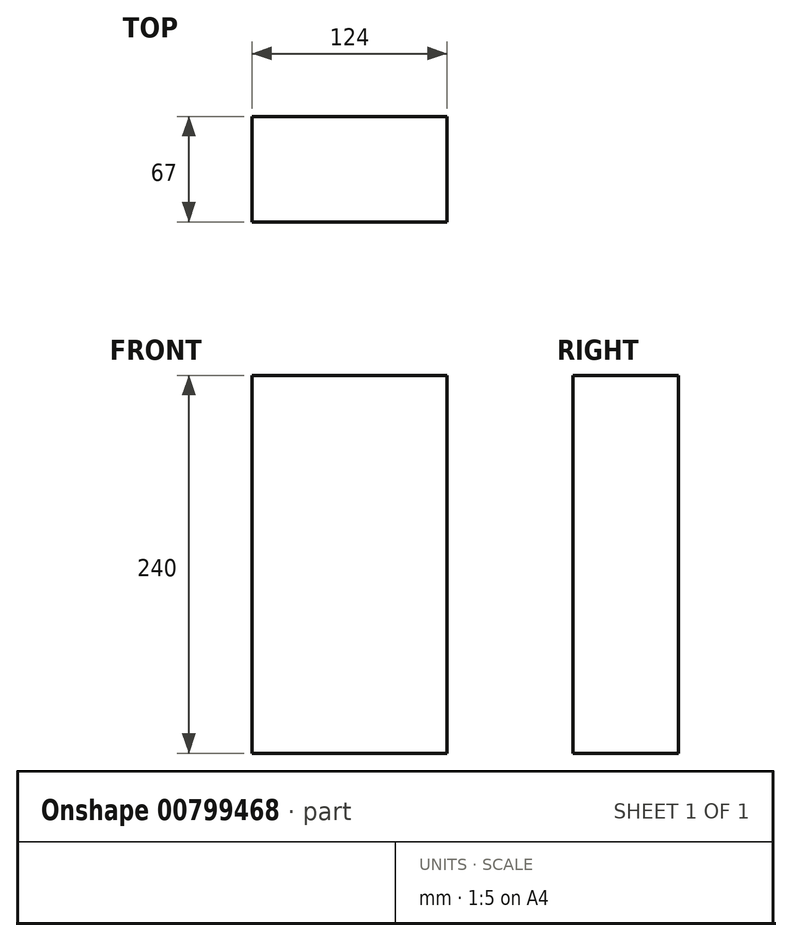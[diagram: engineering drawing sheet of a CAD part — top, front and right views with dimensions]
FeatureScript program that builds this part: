
annotation { "Feature Type Name" : "Feature", "Feature Type Description" : "" }
export const myFeature = defineFeature(function(context is Context, id is Id, definition is map)
    precondition{}
    {
        {
            var Q0;
            Q0=qCreatedBy(makeId("Front.planeOp"),FACE);
            var sketch = newSketch(context, id + "F0", { "sketchPlane" : qUnion([Q0])});
            skLineSegment(sketch, "E0.bottom", {"start": v(0, 0) * mm, "end": v(124, 0) * mm});
            skLineSegment(sketch, "E0.top", {"start": v(0, 240) * mm, "end": v(124, 240) * mm});
            skLineSegment(sketch, "E0.left", {"start": v(0, 0) * mm, "end": v(0, 240) * mm});
            skLineSegment(sketch, "E0.right", {"start": v(124, 0) * mm, "end": v(124, 240) * mm});
            skSolve(sketch);
        }
        {
            var Q0;
            Q0=makeQuery(id+"F0.imprint","IMPRINT",FACE,{"disambiguationData":[TD([[makeQuery(id+"F0.imprint","IMPRINT",EDGE,{"derivedFrom":sQuery(id+"F0.wireOp",EDGE,"E0.bottom")}),1.0]])]});
            extrude(context, id + "F1", {"entities" : qUnion([Q0]), "depth" : 67 * mm, "offsetDistance" : 25 * mm});
        }
    });
